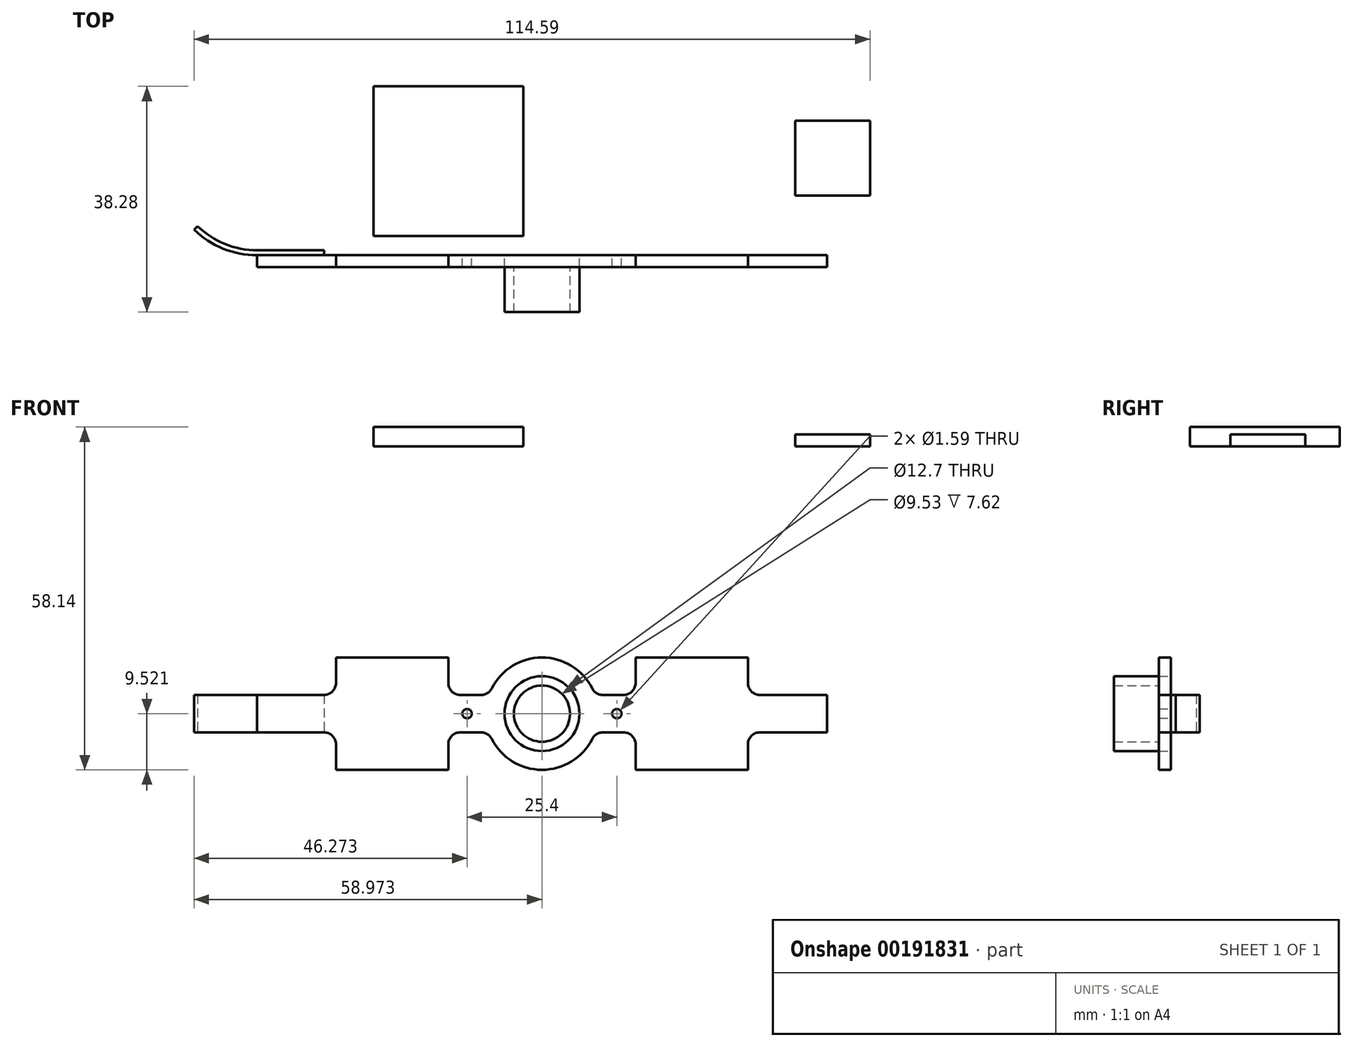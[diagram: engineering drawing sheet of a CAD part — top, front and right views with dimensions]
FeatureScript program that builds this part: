
annotation { "Feature Type Name" : "Feature", "Feature Type Description" : "" }
export const myFeature = defineFeature(function(context is Context, id is Id, definition is map)
    precondition{}
    {
        {
            var Q0;
            Q0=qCreatedBy(makeId("Top.planeOp"),FACE);
            var sketch = newSketch(context, id + "F0", { "sketchPlane" : qUnion([Q0])});
            skLineSegment(sketch, "E0.bottom", {"start": v(-36.5, 28.63) * mm, "end": v(-11.1, 28.63) * mm});
            skLineSegment(sketch, "E0.top", {"start": v(-36.5, 3.23) * mm, "end": v(-11.1, 3.23) * mm});
            skLineSegment(sketch, "E0.left", {"start": v(-36.5, 28.63) * mm, "end": v(-36.5, 3.23) * mm});
            skLineSegment(sketch, "E0.right", {"start": v(-11.1, 28.63) * mm, "end": v(-11.1, 3.23) * mm});
            skSolve(sketch);
        }
        {
            var Q0;
            Q0=makeQuery(id+"F0.imprint","IMPRINT",FACE,{"disambiguationData":[TD([[makeQuery(id+"F0.imprint","IMPRINT",EDGE,{"derivedFrom":sQuery(id+"F0.wireOp",EDGE,"E0.bottom")}),-1.0]])]});
            extrude(context, id + "F1", {"entities" : qUnion([Q0]), "depth" : 3.3 * mm});
        }
        {
            var Q0;
            Q0=qCreatedBy(makeId("Top.planeOp"),FACE);
            var sketch = newSketch(context, id + "F2", { "sketchPlane" : qUnion([Q0])});
            skLineSegment(sketch, "E1.bottom", {"start": v(35, 22.8) * mm, "end": v(47.7, 22.8) * mm});
            skLineSegment(sketch, "E1.top", {"start": v(35, 10.1) * mm, "end": v(47.7, 10.1) * mm});
            skLineSegment(sketch, "E1.left", {"start": v(35, 22.8) * mm, "end": v(35, 10.1) * mm});
            skLineSegment(sketch, "E1.right", {"start": v(47.7, 22.8) * mm, "end": v(47.7, 10.1) * mm});
            skSolve(sketch);
        }
        {
            var Q0;
            Q0=makeQuery(id+"F2.imprint","IMPRINT",FACE,{"disambiguationData":[TD([[makeQuery(id+"F2.imprint","IMPRINT",EDGE,{"derivedFrom":sQuery(id+"F2.wireOp",EDGE,"E1.bottom")}),-1.0]])]});
            extrude(context, id + "F3", {"entities" : qUnion([Q0]), "depth" : 2.03 * mm});
        }
        {
            var Q0;
            Q0=qCreatedBy(makeId("Front.planeOp"),FACE);
            var sketch = newSketch(context, id + "F4", { "sketchPlane" : qUnion([Q0])});
            skLineSegment(sketch, "E2.bottom", {"start": v(-56.23, -42.14) * mm, "end": v(-44.87, -42.14) * mm});
            skLineSegment(sketch, "E2.top", {"start": v(-56.23, -48.5) * mm, "end": v(-44.87, -48.5) * mm});
            skLineSegment(sketch, "E2.left", {"start": v(-56.23, -42.14) * mm, "end": v(-56.23, -48.5) * mm});
            skLineSegment(sketch, "E2.right", {"start": v(40.4, -42.14) * mm, "end": v(40.4, -48.5) * mm});
            skLineSegment(sketch, "E3", {"start": v(-7.92, -42.14) * mm, "end": v(-7.92, -48.5) * mm, "construction": true});
            skArc(sketch, "E4", {"start": v(-16.42, -49.61) * mm, "mid": v(-7.92, -54.84) * mm, "end": v(0.59, -49.61) * mm});
            skCircle(sketch, "E5", {"center": v(-7.92, -45.32) * mm, "radius": 6.35 * mm});
            skLineSegment(sketch, "E6.trimOffspring", {"start": v(2.4, -48.5) * mm, "end": v(5.93, -48.5) * mm});
            skLineSegment(sketch, "E7.trimOffspring", {"start": v(2.4, -42.14) * mm, "end": v(5.93, -42.14) * mm});
            skArc(sketch, "E8.trimOffspring", {"start": v(0.59, -41.03) * mm, "mid": v(-7.92, -35.8) * mm, "end": v(-16.42, -41.03) * mm});
            skLineSegment(sketch, "E9", {"start": v(-56.23, -45.32) * mm, "end": v(40.4, -45.32) * mm, "construction": true});
            skLineSegment(sketch, "E10.bottom", {"start": v(-23.8, -35.8) * mm, "end": v(-42.84, -35.8) * mm});
            skLineSegment(sketch, "E10.top", {"start": v(-23.8, -54.84) * mm, "end": v(-42.84, -54.84) * mm});
            skLineSegment(sketch, "E10.left", {"start": v(-23.8, -35.8) * mm, "end": v(-23.8, -40.11) * mm});
            skLineSegment(sketch, "E10.right", {"start": v(-42.84, -35.8) * mm, "end": v(-42.84, -40.11) * mm});
            skPoint(sketch, "E10.middle", {"position": v(-33.32, -45.32) * mm});
            skLineSegment(sketch, "E11.MirrorCS", {"start": v(7.96, -35.8) * mm, "end": v(7.96, -40.11) * mm});
            skLineSegment(sketch, "E12.MirrorCS", {"start": v(7.96, -35.8) * mm, "end": v(27, -35.8) * mm});
            skLineSegment(sketch, "E13.MirrorCS", {"start": v(27, -35.8) * mm, "end": v(27, -40.11) * mm});
            skLineSegment(sketch, "E14.MirrorCS", {"start": v(7.96, -54.84) * mm, "end": v(27, -54.84) * mm});
            skLineSegment(sketch, "E15.trimOffspring", {"start": v(-42.84, -50.53) * mm, "end": v(-42.84, -54.84) * mm});
            skLineSegment(sketch, "E16.trimOffspring", {"start": v(-21.76, -42.14) * mm, "end": v(-18.23, -42.14) * mm});
            skLineSegment(sketch, "E17.trimOffspring", {"start": v(-23.8, -50.53) * mm, "end": v(-23.8, -54.84) * mm});
            skLineSegment(sketch, "E18.trimOffspring", {"start": v(-21.76, -48.5) * mm, "end": v(-18.23, -48.5) * mm});
            skLineSegment(sketch, "E19.trimOffspring", {"start": v(7.96, -50.53) * mm, "end": v(7.96, -54.84) * mm});
            skLineSegment(sketch, "E20.trimOffspring", {"start": v(29.04, -48.5) * mm, "end": v(40.4, -48.5) * mm});
            skLineSegment(sketch, "E21.trimOffspring", {"start": v(27, -50.53) * mm, "end": v(27, -54.84) * mm});
            skLineSegment(sketch, "E22.trimOffspring", {"start": v(29.04, -42.14) * mm, "end": v(40.4, -42.14) * mm});
            skPoint(sketch, "E23.visualSharp", {"position": v(-16.9, -42.14) * mm});
            skArc(sketch, "E23.filletArc", {"start": v(-18.23, -42.14) * mm, "mid": v(-17.17, -41.84) * mm, "end": v(-16.42, -41.03) * mm});
            skPoint(sketch, "E24.visualSharp", {"position": v(-23.8, -42.14) * mm});
            skArc(sketch, "E24.filletArc", {"start": v(-23.8, -40.11) * mm, "mid": v(-23.2, -41.55) * mm, "end": v(-21.76, -42.14) * mm});
            skPoint(sketch, "E25.visualSharp", {"position": v(-23.8, -48.5) * mm});
            skArc(sketch, "E25.filletArc", {"start": v(-21.76, -48.5) * mm, "mid": v(-23.2, -49.09) * mm, "end": v(-23.8, -50.53) * mm});
            skPoint(sketch, "E26.visualSharp", {"position": v(-42.84, -48.5) * mm});
            skArc(sketch, "E26.filletArc", {"start": v(-42.84, -50.53) * mm, "mid": v(-43.44, -49.09) * mm, "end": v(-44.87, -48.5) * mm});
            skPoint(sketch, "E27.visualSharp", {"position": v(-42.84, -42.14) * mm});
            skArc(sketch, "E27.filletArc", {"start": v(-44.87, -42.14) * mm, "mid": v(-43.44, -41.55) * mm, "end": v(-42.84, -40.11) * mm});
            skPoint(sketch, "E28.visualSharp", {"position": v(7.96, -42.14) * mm});
            skArc(sketch, "E28.filletArc", {"start": v(5.93, -42.14) * mm, "mid": v(7.36, -41.55) * mm, "end": v(7.96, -40.11) * mm});
            skPoint(sketch, "E29.visualSharp", {"position": v(27, -42.14) * mm});
            skArc(sketch, "E29.filletArc", {"start": v(27, -40.11) * mm, "mid": v(27.6, -41.55) * mm, "end": v(29.04, -42.14) * mm});
            skPoint(sketch, "E30.visualSharp", {"position": v(27, -48.5) * mm});
            skArc(sketch, "E30.filletArc", {"start": v(29.04, -48.5) * mm, "mid": v(27.6, -49.09) * mm, "end": v(27, -50.53) * mm});
            skPoint(sketch, "E31.visualSharp", {"position": v(7.96, -48.5) * mm});
            skArc(sketch, "E31.filletArc", {"start": v(7.96, -50.53) * mm, "mid": v(7.36, -49.09) * mm, "end": v(5.93, -48.5) * mm});
            skPoint(sketch, "E32.visualSharp", {"position": v(1.06, -42.14) * mm});
            skArc(sketch, "E32.filletArc", {"start": v(0.59, -41.03) * mm, "mid": v(1.34, -41.84) * mm, "end": v(2.4, -42.14) * mm});
            skPoint(sketch, "E33.visualSharp", {"position": v(-16.9, -48.5) * mm});
            skArc(sketch, "E33.filletArc", {"start": v(-16.42, -49.61) * mm, "mid": v(-17.17, -48.8) * mm, "end": v(-18.23, -48.5) * mm});
            skPoint(sketch, "E34.visualSharp", {"position": v(1.06, -48.5) * mm});
            skArc(sketch, "E34.filletArc", {"start": v(2.4, -48.5) * mm, "mid": v(1.34, -48.8) * mm, "end": v(0.59, -49.61) * mm});
            skCircle(sketch, "E35", {"center": v(-20.62, -45.32) * mm, "radius": 0.8 * mm});
            skCircle(sketch, "E36.MirrorC", {"center": v(4.78, -45.32) * mm, "radius": 0.8 * mm});
            skSolve(sketch);
        }
        {
            var Q0;
            Q0 = qSketchRegion(id + "F4", true);
            extrude(context, id + "F5", {"entities" : qUnion([Q0]), "depth" : 2.03 * mm});
        }
        {
            var Q0;
            Q0=makeQuery(id+"F5.opExtrude","SWEPT_FACE",FACE,{"disambiguationData":[OSD([sQuery(id+"F4.wireOp",EDGE,"E2.top")])]});
            var sketch = newSketch(context, id + "F6", { "sketchPlane" : qUnion([Q0])});
            skLineSegment(sketch, "E37", {"start": v(-44.87, 0) * mm, "end": v(-56.23, 0) * mm});
            skArc(sketch, "E38", {"start": v(-56.23, 0) * mm, "mid": v(-61.98, -1.12) * mm, "end": v(-66.9, -4.32) * mm});
            skArc(sketch, "E39.0", {"start": v(-56.23, -0.84) * mm, "mid": v(-61.67, -1.9) * mm, "end": v(-66.31, -4.92) * mm});
            skLineSegment(sketch, "E39.1", {"start": v(-44.87, -0.84) * mm, "end": v(-56.23, -0.84) * mm});
            skLineSegment(sketch, "E40", {"start": v(-44.87, 0) * mm, "end": v(-44.87, -0.84) * mm});
            skLineSegment(sketch, "E41", {"start": v(-66.31, -4.92) * mm, "end": v(-66.9, -4.32) * mm});
            skSolve(sketch);
        }
        {
            var Q0;
            Q0 = qSketchRegion(id + "F6", true);
            extrude(context, id + "F7", {"entities" : qUnion([Q0]), "oppositeDirection" : true, "depth" : 6.35 * mm});
        }
        {
            var Q0;
            Q0=qCreatedBy(makeId("Top.planeOp"),FACE);
            var sketch = newSketch(context, id + "F8", { "sketchPlane" : qUnion([Q0])});
            skCircle(sketch, "E42", {"center": v(7.02, 0) * mm, "radius": 0.25 * mm});
            skSolve(sketch);
        }
        {
            var Q0;
            Q0 = qSketchRegion(id + "F8", true);
            extrude(context, id + "F9", {"entities" : qUnion([Q0]), "depth" : 15.88 * mm});
        }
        {
            var Q0;
            Q0=makeQuery(id+"F5.opExtrude","CAP_FACE",FACE,{"disambiguationData":[OSD([sQuery(id+"F4.wireOp",EDGE,"E2.bottom"),sQuery(id+"F4.wireOp",EDGE,"E2.top"),sQuery(id+"F4.wireOp",EDGE,"E2.left"),sQuery(id+"F4.wireOp",EDGE,"E2.right"),sQuery(id+"F4.wireOp",EDGE,"E4"),sQuery(id+"F4.wireOp",EDGE,"E5"),sQuery(id+"F4.wireOp",EDGE,"E6.trimOffspring"),sQuery(id+"F4.wireOp",EDGE,"E7.trimOffspring"),sQuery(id+"F4.wireOp",EDGE,"E8.trimOffspring"),sQuery(id+"F4.wireOp",EDGE,"E10.bottom"),sQuery(id+"F4.wireOp",EDGE,"E10.top"),sQuery(id+"F4.wireOp",EDGE,"E10.left"),sQuery(id+"F4.wireOp",EDGE,"E10.right"),sQuery(id+"F4.wireOp",EDGE,"E11.MirrorCS"),sQuery(id+"F4.wireOp",EDGE,"E12.MirrorCS"),sQuery(id+"F4.wireOp",EDGE,"E13.MirrorCS"),sQuery(id+"F4.wireOp",EDGE,"E14.MirrorCS"),sQuery(id+"F4.wireOp",EDGE,"E15.trimOffspring"),sQuery(id+"F4.wireOp",EDGE,"E16.trimOffspring"),sQuery(id+"F4.wireOp",EDGE,"E17.trimOffspring"),sQuery(id+"F4.wireOp",EDGE,"E18.trimOffspring"),sQuery(id+"F4.wireOp",EDGE,"E19.trimOffspring"),sQuery(id+"F4.wireOp",EDGE,"E20.trimOffspring"),sQuery(id+"F4.wireOp",EDGE,"E21.trimOffspring"),sQuery(id+"F4.wireOp",EDGE,"E22.trimOffspring"),sQuery(id+"F4.wireOp",EDGE,"E23.filletArc"),sQuery(id+"F4.wireOp",EDGE,"E24.filletArc"),sQuery(id+"F4.wireOp",EDGE,"E25.filletArc"),sQuery(id+"F4.wireOp",EDGE,"E26.filletArc"),sQuery(id+"F4.wireOp",EDGE,"E27.filletArc"),sQuery(id+"F4.wireOp",EDGE,"E28.filletArc"),sQuery(id+"F4.wireOp",EDGE,"E29.filletArc"),sQuery(id+"F4.wireOp",EDGE,"E30.filletArc"),sQuery(id+"F4.wireOp",EDGE,"E31.filletArc"),sQuery(id+"F4.wireOp",EDGE,"E32.filletArc"),sQuery(id+"F4.wireOp",EDGE,"E33.filletArc"),sQuery(id+"F4.wireOp",EDGE,"E34.filletArc"),sQuery(id+"F4.wireOp",EDGE,"E35"),sQuery(id+"F4.wireOp",EDGE,"E36.MirrorC")])],"isStart":false});
            var sketch = newSketch(context, id + "F10", { "sketchPlane" : qUnion([Q0])});
            skCircle(sketch, "E43", {"center": v(-7.92, -45.32) * mm, "radius": 6.35 * mm});
            skCircle(sketch, "E44", {"center": v(-7.92, -45.32) * mm, "radius": 4.76 * mm});
            skSolve(sketch);
        }
        {
            var Q0;
            Q0 = qSketchRegion(id + "F10", true);
            extrude(context, id + "F11", {"entities" : qUnion([Q0]), "depth" : 7.62 * mm});
        }
        {
            var Q0;
            Q0=makeQuery(id+"F9.opExtrude","SWEPT_BODY",BODY,{"disambiguationData":[OSD([sQuery(id+"F8.wireOp",EDGE,"E42")])]});
            deleteBodies(context, id + "F12", {"entities" : qUnion([Q0])});
        }
    });
